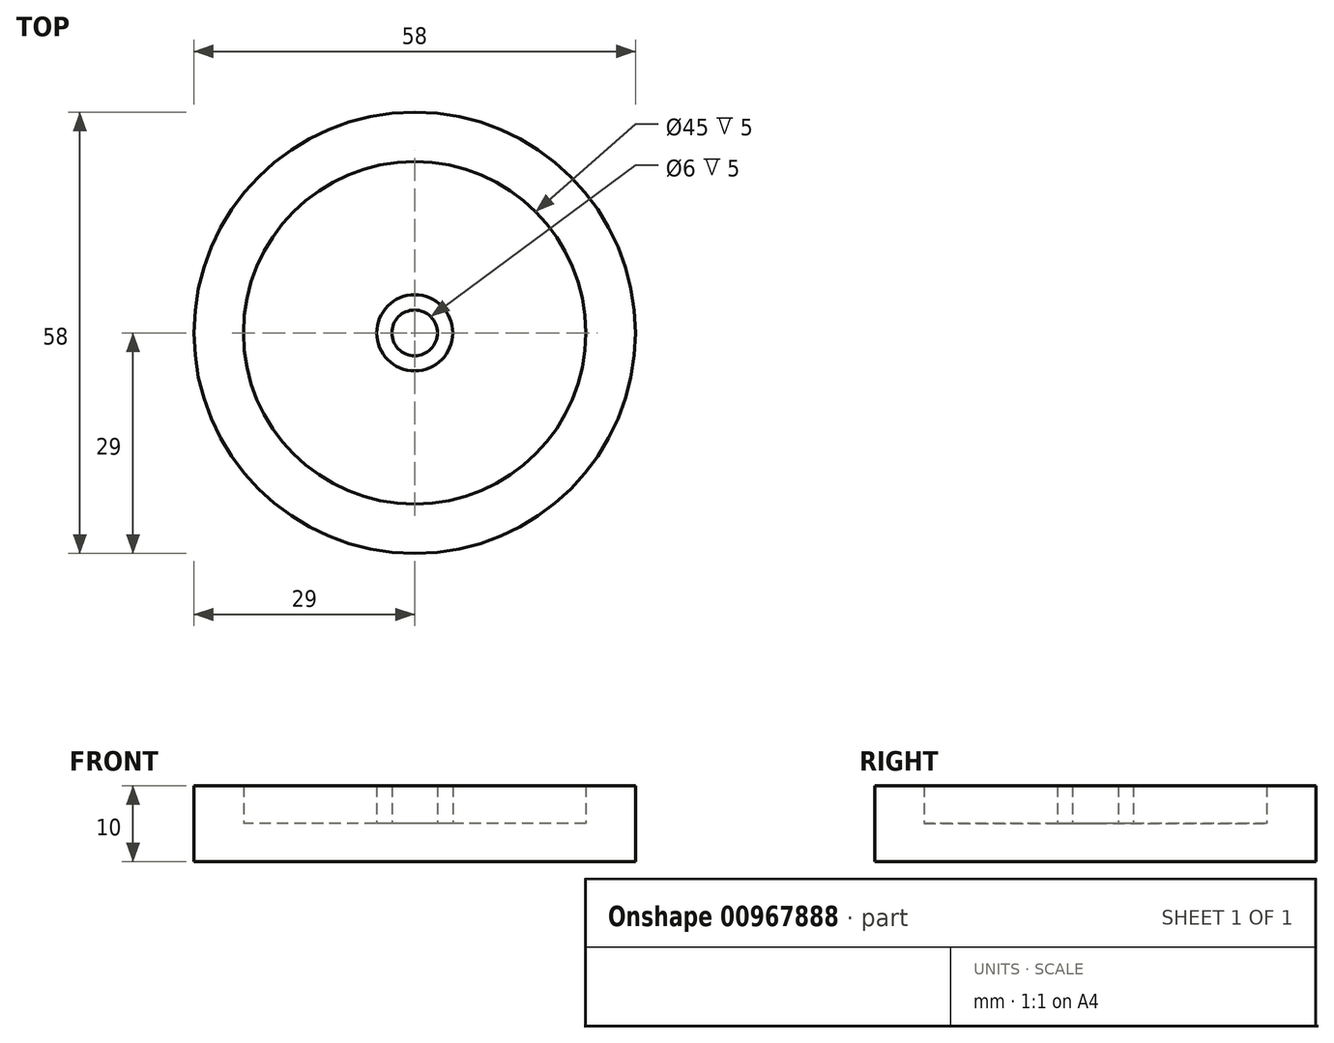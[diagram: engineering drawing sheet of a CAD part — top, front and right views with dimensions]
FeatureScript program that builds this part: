
annotation { "Feature Type Name" : "Feature", "Feature Type Description" : "" }
export const myFeature = defineFeature(function(context is Context, id is Id, definition is map)
    precondition{}
    {
        {
            var Q0;
            Q0=qCreatedBy(makeId("Top.planeOp"),FACE);
            var sketch = newSketch(context, id + "F0", { "sketchPlane" : qUnion([Q0])});
            skCircle(sketch, "E0", {"center": v(0, 0) * mm, "radius": 29 * mm});
            skCircle(sketch, "E1", {"center": v(0, 0) * mm, "radius": 22.5 * mm});
            skCircle(sketch, "E2", {"center": v(0, 0) * mm, "radius": 5 * mm});
            skCircle(sketch, "E3", {"center": v(0, 0) * mm, "radius": 3 * mm});
            skSolve(sketch);
        }
        {
            var Q0;
            Q0 = qSketchRegion(id + "F0", true);
            var Q1;
            Q1=makeQuery(id+"F0.imprint","IMPRINT",FACE,{"disambiguationData":[TD([[makeQuery(id+"F0.imprint","IMPRINT",EDGE,{"derivedFrom":sQuery(id+"F0.wireOp",EDGE,"E1")}),1.0]])]});
            var Q2;
            Q2=makeQuery(id+"F0.imprint","IMPRINT",FACE,{"disambiguationData":[TD([[makeQuery(id+"F0.imprint","IMPRINT",EDGE,{"derivedFrom":sQuery(id+"F0.wireOp",EDGE,"E2")}),1.0]])]});
            var Q3;
            Q3=makeQuery(id+"F0.imprint","IMPRINT",FACE,{"disambiguationData":[TD([[makeQuery(id+"F0.imprint","IMPRINT",EDGE,{"derivedFrom":sQuery(id+"F0.wireOp",EDGE,"E3")}),1.0]])]});
            extrude(context, id + "F1", {"entities" : qUnion([Q0, Q1, Q2, Q3]), "depth" : 5 * mm, "offsetDistance" : 25 * mm});
        }
        {
            var Q0;
            Q0 = qSketchRegion(id + "F0", true);
            var Q1;
            Q1=makeQuery(id+"F0.imprint","IMPRINT",FACE,{"disambiguationData":[TD([[makeQuery(id+"F0.imprint","IMPRINT",EDGE,{"derivedFrom":sQuery(id+"F0.wireOp",EDGE,"E2")}),1.0]])]});
            extrude(context, id + "F2", {"entities" : qUnion([Q0, Q1]), "operationType" : NewBodyOperationType.ADD, "depth" : 10 * mm, "offsetDistance" : 25 * mm});
        }
    });
